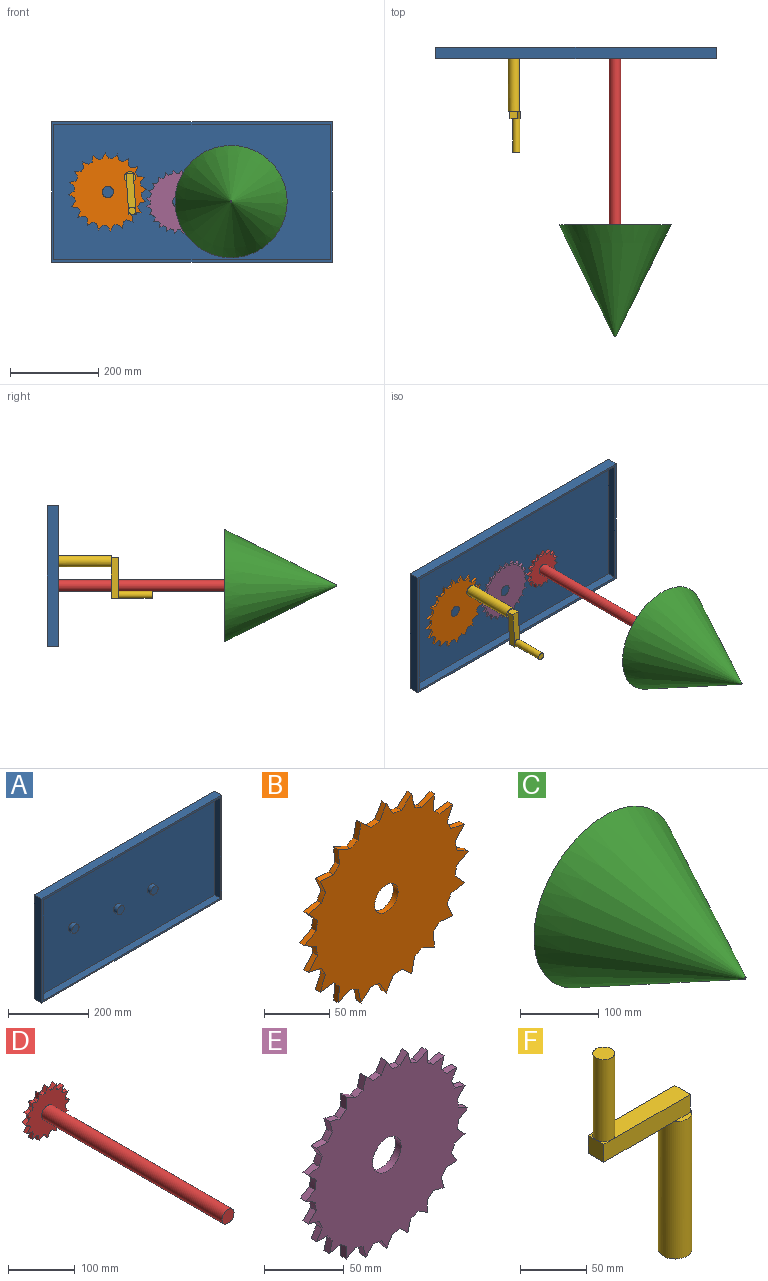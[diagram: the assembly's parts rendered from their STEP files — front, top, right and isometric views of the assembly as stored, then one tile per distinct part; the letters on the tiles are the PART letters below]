
ASSEMBLY  parts=6 mates=5
PART A: 17 faces, bbox 635x25.4x317.5 mm
  f0: plane 635x317.5mm, normal (0,-1,0), area 9574.2mm2, adj f1,f2,f3,f4,f6,f7,f8,f9
  f1: plane 317.5x25.4mm, normal (1,0,0), area 8064.5mm2, adj f0,f2,f4,f5
  f2: plane 635x25.4mm, normal (0,0,1), area 16129mm2, adj f0,f1,f3,f5
  f3: plane 317.5x25.4mm, normal (-1,0,0), area 8064.5mm2, adj f0,f2,f4,f5
  f4: plane 635x25.4mm, normal (0,0,-1), area 16129mm2, adj f0,f1,f3,f5
  f5: plane 635x317.5mm, normal (0,1,0), area 201612.5mm2, adj f1,f2,f3,f4
  f6: plane 307.34x20.32mm, normal (-1,0,0), area 6245.1mm2, adj f0,f7,f9,f10
  f7: plane 624.84x20.32mm, normal (0,0,-1), area 12696.7mm2, adj f0,f6,f8,f10
  f8: plane 307.34x20.32mm, normal (1,0,0), area 6245.1mm2, adj f0,f7,f9,f10
  f9: plane 624.84x20.32mm, normal (0,0,1), area 12696.7mm2, adj f0,f6,f8,f10
  f10: plane 624.84x307.34mm, normal (0,-1,0), area 190518.2mm2, adj f6,f7,f8,f9,f11,f13,f15
  f11: cylinder r=12.7mm len=25.4mm, axis (0,1,0), area 1013.4mm2, adj f10,f12
  f12: plane 25.4x25.4mm, normal (0,-1,0), area 506.7mm2, adj f11
  f13: cylinder r=12.7mm len=25.4mm, axis (0,1,0), area 1013.4mm2, adj f10,f14
  f14: plane 25.4x25.4mm, normal (0,-1,0), area 506.7mm2, adj f13
  f15: cylinder r=12.7mm len=25.4mm, axis (0,1,0), area 1013.4mm2, adj f10,f16
  f16: plane 25.4x25.4mm, normal (0,-1,0), area 506.7mm2, adj f15
PART B: 63 faces, bbox 177.4x5.1x177.4 mm
  f0: cylinder r=76.2mm len=8.92mm, axis (0,1,0), area 45.9mm2, adj f20,f21,f22,f60
  f1: cylinder r=76.2mm len=8.05mm, axis (0,1,0), area 45.9mm2, adj f20,f21,f58,f61
  f2: cylinder r=76.2mm len=6.39mm, axis (0,1,0), area 45.9mm2, adj f20,f21,f56,f59
  f3: cylinder r=76.2mm len=8.05mm, axis (0,1,0), area 45.9mm2, adj f20,f21,f54,f57
  f4: cylinder r=76.2mm len=8.92mm, axis (0,1,0), area 45.9mm2, adj f20,f21,f52,f55
  f5: cylinder r=76.2mm len=8.92mm, axis (0,1,0), area 45.9mm2, adj f20,f21,f50,f53
  f6: cylinder r=76.2mm len=8.05mm, axis (0,1,0), area 45.9mm2, adj f20,f21,f48,f51
  f7: cylinder r=76.2mm len=6.39mm, axis (0,1,0), area 45.9mm2, adj f20,f21,f46,f49
  f8: cylinder r=76.2mm len=8.05mm, axis (0,1,0), area 45.9mm2, adj f20,f21,f44,f47
  f9: cylinder r=76.2mm len=8.92mm, axis (0,1,0), area 45.9mm2, adj f20,f21,f42,f45
  f10: cylinder r=76.2mm len=8.92mm, axis (0,1,0), area 45.9mm2, adj f20,f21,f40,f43
  f11: cylinder r=76.2mm len=8.05mm, axis (0,1,0), area 45.9mm2, adj f20,f21,f38,f41
  f12: cylinder r=76.2mm len=6.39mm, axis (0,1,0), area 45.9mm2, adj f20,f21,f36,f39
  f13: cylinder r=76.2mm len=8.05mm, axis (0,1,0), area 45.9mm2, adj f20,f21,f34,f37
  f14: cylinder r=76.2mm len=8.92mm, axis (0,1,0), area 45.9mm2, adj f20,f21,f32,f35
  f15: cylinder r=76.2mm len=8.92mm, axis (0,1,0), area 45.9mm2, adj f20,f21,f30,f33
  f16: cylinder r=76.2mm len=8.05mm, axis (0,1,0), area 45.9mm2, adj f20,f21,f28,f31
  f17: cylinder r=76.2mm len=6.39mm, axis (0,1,0), area 45.9mm2, adj f20,f21,f26,f29
  f18: cylinder r=76.2mm len=8.05mm, axis (0,1,0), area 45.9mm2, adj f20,f21,f24,f27
  f19: cylinder r=76.2mm len=8.92mm, axis (0,1,0), area 45.9mm2, adj f20,f21,f23,f25
  f20: plane 177.44x177.44mm, normal (0,-1,0), area 19578.6mm2, adj f0,f1,f2,f3,f4,f5,f6,f7
  f21: plane 177.44x177.44mm, normal (0,1,0), area 19578.6mm2, adj f0,f1,f2,f3,f4,f5,f6,f7
  f22: plane 12.88x7.44mm, normal (0.87,0,0.5), area 75.6mm2, adj f0,f20,f21,f23
  f23: plane 12.88x7.44mm, normal (-0.87,0,0.5), area 75.6mm2, adj f19,f20,f21,f22
  f24: plane 14.55x5.08mm, normal (-0.98,0,0.21), area 75.6mm2, adj f18,f20,f21,f25
  f25: plane 11.05x9.95mm, normal (0.67,0,0.74), area 75.6mm2, adj f19,f20,f21,f24
  f26: plane 14.79x5.08mm, normal (-0.99,0,-0.1), area 75.6mm2, adj f17,f20,f21,f27
  f27: plane 13.59x6.05mm, normal (0.41,0,0.91), area 75.6mm2, adj f18,f20,f21,f26
  f28: plane 13.59x6.05mm, normal (-0.91,0,-0.41), area 75.6mm2, adj f16,f20,f21,f29
  f29: plane 14.79x5.08mm, normal (0.1,0,0.99), area 75.6mm2, adj f17,f20,f21,f28
  f30: plane 11.05x9.95mm, normal (-0.74,0,-0.67), area 75.6mm2, adj f15,f20,f21,f31
  f31: plane 14.55x5.08mm, normal (-0.21,0,0.98), area 75.6mm2, adj f16,f20,f21,f30
  f32: plane 12.88x7.44mm, normal (-0.5,0,-0.87), area 75.6mm2, adj f14,f20,f21,f33
  f33: plane 12.88x7.44mm, normal (-0.5,0,0.87), area 75.6mm2, adj f15,f20,f21,f32
  f34: plane 14.55x5.08mm, normal (-0.21,0,-0.98), area 75.6mm2, adj f13,f20,f21,f35
  f35: plane 11.05x9.95mm, normal (-0.74,0,0.67), area 75.6mm2, adj f14,f20,f21,f34
  f36: plane 14.79x5.08mm, normal (0.1,0,-0.99), area 75.6mm2, adj f12,f20,f21,f37
  f37: plane 13.59x6.05mm, normal (-0.91,0,0.41), area 75.6mm2, adj f13,f20,f21,f36
  f38: plane 13.59x6.05mm, normal (0.41,0,-0.91), area 75.6mm2, adj f11,f20,f21,f39
  f39: plane 14.79x5.08mm, normal (-0.99,0,0.1), area 75.6mm2, adj f12,f20,f21,f38
  f40: plane 11.05x9.95mm, normal (0.67,0,-0.74), area 75.6mm2, adj f10,f20,f21,f41
  f41: plane 14.55x5.08mm, normal (-0.98,0,-0.21), area 75.6mm2, adj f11,f20,f21,f40
  f42: plane 12.88x7.44mm, normal (0.87,0,-0.5), area 75.6mm2, adj f9,f20,f21,f43
  f43: plane 12.88x7.44mm, normal (-0.87,0,-0.5), area 75.6mm2, adj f10,f20,f21,f42
  f44: plane 14.55x5.08mm, normal (0.98,0,-0.21), area 75.6mm2, adj f8,f20,f21,f45
  f45: plane 11.05x9.95mm, normal (-0.67,0,-0.74), area 75.6mm2, adj f9,f20,f21,f44
  f46: plane 14.79x5.08mm, normal (0.99,0,0.1), area 75.6mm2, adj f7,f20,f21,f47
  f47: plane 13.59x6.05mm, normal (-0.41,0,-0.91), area 75.6mm2, adj f8,f20,f21,f46
  f48: plane 13.59x6.05mm, normal (0.91,0,0.41), area 75.6mm2, adj f6,f20,f21,f49
  f49: plane 14.79x5.08mm, normal (-0.1,0,-0.99), area 75.6mm2, adj f7,f20,f21,f48
  f50: plane 11.05x9.95mm, normal (0.74,0,0.67), area 75.6mm2, adj f5,f20,f21,f51
  f51: plane 14.55x5.08mm, normal (0.21,0,-0.98), area 75.6mm2, adj f6,f20,f21,f50
  f52: plane 12.88x7.44mm, normal (0.5,0,0.87), area 75.6mm2, adj f4,f20,f21,f53
  f53: plane 12.88x7.44mm, normal (0.5,0,-0.87), area 75.6mm2, adj f5,f20,f21,f52
  f54: plane 14.55x5.08mm, normal (0.21,0,0.98), area 75.6mm2, adj f3,f20,f21,f55
  f55: plane 11.05x9.95mm, normal (0.74,0,-0.67), area 75.6mm2, adj f4,f20,f21,f54
  f56: plane 14.79x5.08mm, normal (-0.1,0,0.99), area 75.6mm2, adj f2,f20,f21,f57
  f57: plane 13.59x6.05mm, normal (0.91,0,-0.41), area 75.6mm2, adj f3,f20,f21,f56
  f58: plane 13.59x6.05mm, normal (-0.41,0,0.91), area 75.6mm2, adj f1,f20,f21,f59
  f59: plane 14.79x5.08mm, normal (0.99,0,-0.1), area 75.6mm2, adj f2,f20,f21,f58
  f60: plane 11.05x9.95mm, normal (-0.67,0,0.74), area 75.6mm2, adj f0,f20,f21,f61
  f61: plane 14.55x5.08mm, normal (0.98,0,0.21), area 75.6mm2, adj f1,f20,f21,f60
  f62: cylinder r=12.7mm len=25.4mm, axis (0,-1,0), area 405.4mm2, adj f20,f21
PART C: 3 faces, bbox 254x254x254 mm
  f0: plane 254x254mm, normal (0,1,0), area 50670.7mm2, adj f2
  f1: plane 2.54x2.54mm, normal (0,-1,0), area 5.1mm2, adj f2
  f2: cone r=127mm half-angle=26.3deg, axis (0,1,0), area 114208.3mm2, adj f0,f1
PART D: 54 faces, bbox 93.1x388.6x93.1 mm
  f0: cylinder r=12.7mm len=25.4mm, axis (0,-1,0), area 405.4mm2, adj f17,f51
  f1: cylinder r=38.1mm len=7.62mm, axis (0,1,0), area 36.4mm2, adj f17,f47,f48,f50
  f2: cylinder r=38.1mm len=7.62mm, axis (0,1,0), area 36.4mm2, adj f17,f18,f49,f50
  f3: cylinder r=38.1mm len=7.62mm, axis (0,1,0), area 36.4mm2, adj f17,f45,f46,f50
  f4: cylinder r=38.1mm len=7.62mm, axis (0,1,0), area 36.4mm2, adj f17,f43,f44,f50
  f5: cylinder r=38.1mm len=7.62mm, axis (0,1,0), area 36.4mm2, adj f17,f41,f42,f50
  f6: cylinder r=38.1mm len=7.62mm, axis (0,1,0), area 36.4mm2, adj f17,f39,f40,f50
  f7: cylinder r=38.1mm len=7.62mm, axis (0,1,0), area 36.4mm2, adj f17,f37,f38,f50
  f8: cylinder r=38.1mm len=7.62mm, axis (0,1,0), area 36.4mm2, adj f17,f35,f36,f50
  f9: cylinder r=38.1mm len=7.62mm, axis (0,1,0), area 36.4mm2, adj f17,f33,f34,f50
  f10: cylinder r=38.1mm len=7.62mm, axis (0,1,0), area 36.4mm2, adj f17,f31,f32,f50
  f11: cylinder r=38.1mm len=7.62mm, axis (0,1,0), area 36.4mm2, adj f17,f29,f30,f50
  f12: cylinder r=38.1mm len=7.62mm, axis (0,1,0), area 36.4mm2, adj f17,f27,f28,f50
  f13: cylinder r=38.1mm len=7.62mm, axis (0,1,0), area 36.4mm2, adj f17,f25,f26,f50
  f14: cylinder r=38.1mm len=7.62mm, axis (0,1,0), area 36.4mm2, adj f17,f23,f24,f50
  f15: cylinder r=38.1mm len=7.62mm, axis (0,1,0), area 36.4mm2, adj f17,f21,f22,f50
  f16: cylinder r=38.1mm len=7.62mm, axis (0,1,0), area 36.4mm2, adj f17,f19,f20,f50
  f17: plane 93.12x93.12mm, normal (0,1,0), area 4731.9mm2, adj f0,f1,f2,f3,f4,f5,f6,f7
  f18: plane 8.8x7.62mm, normal (0.87,0,0.5), area 77.4mm2, adj f2,f17,f19,f50
  f19: plane 8.8x7.62mm, normal (-0.87,0,0.5), area 77.4mm2, adj f16,f17,f18,f50
  f20: plane 8.06x7.62mm, normal (0.61,0,0.79), area 77.4mm2, adj f16,f17,f21,f50
  f21: plane 10.07x7.62mm, normal (-0.99,0,0.13), area 77.4mm2, adj f15,f17,f20,f50
  f22: plane 9.81x7.62mm, normal (0.26,0,0.97), area 77.4mm2, adj f15,f17,f23,f50
  f23: plane 9.81x7.62mm, normal (-0.97,0,-0.26), area 77.4mm2, adj f14,f17,f22,f50
  f24: plane 10.07x7.62mm, normal (-0.13,0,0.99), area 77.4mm2, adj f14,f17,f25,f50
  f25: plane 8.06x7.62mm, normal (-0.79,0,-0.61), area 77.4mm2, adj f13,f17,f24,f50
  f26: plane 8.8x7.62mm, normal (-0.5,0,0.87), area 77.4mm2, adj f13,f17,f27,f50
  f27: plane 8.8x7.62mm, normal (-0.5,0,-0.87), area 77.4mm2, adj f12,f17,f26,f50
  f28: plane 8.06x7.62mm, normal (-0.79,0,0.61), area 77.4mm2, adj f12,f17,f29,f50
  f29: plane 10.07x7.62mm, normal (-0.13,0,-0.99), area 77.4mm2, adj f11,f17,f28,f50
  f30: plane 9.81x7.62mm, normal (-0.97,0,0.26), area 77.4mm2, adj f11,f17,f31,f50
  f31: plane 9.81x7.62mm, normal (0.26,0,-0.97), area 77.4mm2, adj f10,f17,f30,f50
  f32: plane 10.07x7.62mm, normal (-0.99,0,-0.13), area 77.4mm2, adj f10,f17,f33,f50
  f33: plane 8.06x7.62mm, normal (0.61,0,-0.79), area 77.4mm2, adj f9,f17,f32,f50
  f34: plane 8.8x7.62mm, normal (-0.87,0,-0.5), area 77.4mm2, adj f9,f17,f35,f50
  f35: plane 8.8x7.62mm, normal (0.87,0,-0.5), area 77.4mm2, adj f8,f17,f34,f50
  f36: plane 8.06x7.62mm, normal (-0.61,0,-0.79), area 77.4mm2, adj f8,f17,f37,f50
  f37: plane 10.07x7.62mm, normal (0.99,0,-0.13), area 77.4mm2, adj f7,f17,f36,f50
  f38: plane 9.81x7.62mm, normal (-0.26,0,-0.97), area 77.4mm2, adj f7,f17,f39,f50
  f39: plane 9.81x7.62mm, normal (0.97,0,0.26), area 77.4mm2, adj f6,f17,f38,f50
  f40: plane 10.07x7.62mm, normal (0.13,0,-0.99), area 77.4mm2, adj f6,f17,f41,f50
  f41: plane 8.06x7.62mm, normal (0.79,0,0.61), area 77.4mm2, adj f5,f17,f40,f50
  f42: plane 8.8x7.62mm, normal (0.5,0,-0.87), area 77.4mm2, adj f5,f17,f43,f50
  f43: plane 8.8x7.62mm, normal (0.5,0,0.87), area 77.4mm2, adj f4,f17,f42,f50
  f44: plane 8.06x7.62mm, normal (0.79,0,-0.61), area 77.4mm2, adj f4,f17,f45,f50
  f45: plane 10.07x7.62mm, normal (0.13,0,0.99), area 77.4mm2, adj f3,f17,f44,f50
  f46: plane 9.81x7.62mm, normal (0.97,0,-0.26), area 77.4mm2, adj f3,f17,f47,f50
  f47: plane 9.81x7.62mm, normal (-0.26,0,0.97), area 77.4mm2, adj f1,f17,f46,f50
  f48: plane 10.07x7.62mm, normal (0.99,0,0.13), area 77.4mm2, adj f1,f17,f49,f50
  f49: plane 8.06x7.62mm, normal (-0.61,0,0.79), area 77.4mm2, adj f2,f17,f48,f50
  f50: plane 93.12x93.12mm, normal (0,-1,0), area 4731.9mm2, adj f1,f2,f3,f4,f5,f6,f7,f8
  f51: plane 25.4x25.4mm, normal (0,1,0), area 506.7mm2, adj f0
  f52: cylinder r=12.7mm len=381mm, axis (0,1,0), area 30402.4mm2, adj f50,f53
  f53: plane 25.4x25.4mm, normal (0,-1,0), area 506.7mm2, adj f52
PART E: 75 faces, bbox 143.9x5.1x143.9 mm
  f0: cylinder r=63.81mm len=7.02mm, axis (0,1,0), area 36mm2, adj f24,f25,f27,f72
  f1: cylinder r=63.81mm len=6.54mm, axis (0,1,0), area 36mm2, adj f24,f25,f70,f73
  f2: cylinder r=63.81mm len=5.62mm, axis (0,1,0), area 36mm2, adj f24,f25,f68,f71
  f3: cylinder r=63.81mm len=5.62mm, axis (0,1,0), area 36mm2, adj f24,f25,f66,f69
  f4: cylinder r=63.81mm len=6.54mm, axis (0,1,0), area 36mm2, adj f24,f25,f64,f67
  f5: cylinder r=63.81mm len=7.02mm, axis (0,1,0), area 36mm2, adj f24,f25,f62,f65
  f6: cylinder r=63.81mm len=7.02mm, axis (0,1,0), area 36mm2, adj f24,f25,f60,f63
  f7: cylinder r=63.81mm len=6.54mm, axis (0,1,0), area 36mm2, adj f24,f25,f58,f61
  f8: cylinder r=63.81mm len=5.62mm, axis (0,1,0), area 36mm2, adj f24,f25,f56,f59
  f9: cylinder r=63.81mm len=5.62mm, axis (0,1,0), area 36mm2, adj f24,f25,f54,f57
  f10: cylinder r=63.81mm len=6.54mm, axis (0,1,0), area 36mm2, adj f24,f25,f52,f55
  f11: cylinder r=63.81mm len=7.02mm, axis (0,1,0), area 36mm2, adj f24,f25,f50,f53
  f12: cylinder r=63.81mm len=7.02mm, axis (0,1,0), area 36mm2, adj f24,f25,f48,f51
  f13: cylinder r=63.81mm len=6.54mm, axis (0,1,0), area 36mm2, adj f24,f25,f46,f49
  f14: cylinder r=63.81mm len=5.62mm, axis (0,1,0), area 36mm2, adj f24,f25,f44,f47
  f15: cylinder r=63.81mm len=5.62mm, axis (0,1,0), area 36mm2, adj f24,f25,f42,f45
  f16: cylinder r=63.81mm len=6.54mm, axis (0,1,0), area 36mm2, adj f24,f25,f40,f43
  f17: cylinder r=63.81mm len=7.02mm, axis (0,1,0), area 36mm2, adj f24,f25,f38,f41
  f18: cylinder r=63.81mm len=7.02mm, axis (0,1,0), area 36mm2, adj f24,f25,f36,f39
  f19: cylinder r=63.81mm len=6.54mm, axis (0,1,0), area 36mm2, adj f24,f25,f34,f37
  f20: cylinder r=63.81mm len=5.62mm, axis (0,1,0), area 36mm2, adj f24,f25,f32,f35
  f21: cylinder r=63.81mm len=5.62mm, axis (0,1,0), area 36mm2, adj f24,f25,f30,f33
  f22: cylinder r=63.81mm len=7.02mm, axis (0,1,0), area 36mm2, adj f24,f25,f26,f28
  f23: cylinder r=63.81mm len=6.54mm, axis (0,1,0), area 36mm2, adj f24,f25,f29,f31
  f24: plane 143.92x143.92mm, normal (0,-1,0), area 13219.3mm2, adj f0,f1,f2,f3,f4,f5,f6,f7
  f25: plane 143.92x143.92mm, normal (0,1,0), area 13219.3mm2, adj f0,f1,f2,f3,f4,f5,f6,f7
  f26: plane 8.33x5.08mm, normal (-0.87,0,0.5), area 48.8mm2, adj f22,f24,f25,f27
  f27: plane 8.33x5.08mm, normal (0.87,0,0.5), area 48.8mm2, adj f0,f24,f25,f26
  f28: plane 6.8x6.8mm, normal (0.71,0,0.71), area 48.8mm2, adj f22,f24,f25,f29
  f29: plane 9.29x5.08mm, normal (-0.97,0,0.26), area 48.8mm2, adj f23,f24,f25,f28
  f30: plane 9.61x5.08mm, normal (-1,0,0), area 48.8mm2, adj f21,f24,f25,f31
  f31: plane 8.33x5.08mm, normal (0.5,0,0.87), area 48.8mm2, adj f23,f24,f25,f30
  f32: plane 9.29x5.08mm, normal (-0.97,0,-0.26), area 48.8mm2, adj f20,f24,f25,f33
  f33: plane 9.29x5.08mm, normal (0.26,0,0.97), area 48.8mm2, adj f21,f24,f25,f32
  f34: plane 8.33x5.08mm, normal (-0.87,0,-0.5), area 48.8mm2, adj f19,f24,f25,f35
  f35: plane 9.61x5.08mm, normal (0,0,1), area 48.8mm2, adj f20,f24,f25,f34
  f36: plane 6.8x6.8mm, normal (-0.71,0,-0.71), area 48.8mm2, adj f18,f24,f25,f37
  f37: plane 9.29x5.08mm, normal (-0.26,0,0.97), area 48.8mm2, adj f19,f24,f25,f36
  f38: plane 8.33x5.08mm, normal (-0.5,0,-0.87), area 48.8mm2, adj f17,f24,f25,f39
  f39: plane 8.33x5.08mm, normal (-0.5,0,0.87), area 48.8mm2, adj f18,f24,f25,f38
  f40: plane 9.29x5.08mm, normal (-0.26,0,-0.97), area 48.8mm2, adj f16,f24,f25,f41
  f41: plane 6.8x6.8mm, normal (-0.71,0,0.71), area 48.8mm2, adj f17,f24,f25,f40
  f42: plane 9.61x5.08mm, normal (0,0,-1), area 48.8mm2, adj f15,f24,f25,f43
  f43: plane 8.33x5.08mm, normal (-0.87,0,0.5), area 48.8mm2, adj f16,f24,f25,f42
  f44: plane 9.29x5.08mm, normal (0.26,0,-0.97), area 48.8mm2, adj f14,f24,f25,f45
  f45: plane 9.29x5.08mm, normal (-0.97,0,0.26), area 48.8mm2, adj f15,f24,f25,f44
  f46: plane 8.33x5.08mm, normal (0.5,0,-0.87), area 48.8mm2, adj f13,f24,f25,f47
  f47: plane 9.61x5.08mm, normal (-1,0,0), area 48.8mm2, adj f14,f24,f25,f46
  f48: plane 6.8x6.8mm, normal (0.71,0,-0.71), area 48.8mm2, adj f12,f24,f25,f49
  f49: plane 9.29x5.08mm, normal (-0.97,0,-0.26), area 48.8mm2, adj f13,f24,f25,f48
  f50: plane 8.33x5.08mm, normal (0.87,0,-0.5), area 48.8mm2, adj f11,f24,f25,f51
  f51: plane 8.33x5.08mm, normal (-0.87,0,-0.5), area 48.8mm2, adj f12,f24,f25,f50
  f52: plane 9.29x5.08mm, normal (0.97,0,-0.26), area 48.8mm2, adj f10,f24,f25,f53
  f53: plane 6.8x6.8mm, normal (-0.71,0,-0.71), area 48.8mm2, adj f11,f24,f25,f52
  f54: plane 9.61x5.08mm, normal (1,0,0), area 48.8mm2, adj f9,f24,f25,f55
  f55: plane 8.33x5.08mm, normal (-0.5,0,-0.87), area 48.8mm2, adj f10,f24,f25,f54
  f56: plane 9.29x5.08mm, normal (0.97,0,0.26), area 48.8mm2, adj f8,f24,f25,f57
  f57: plane 9.29x5.08mm, normal (-0.26,0,-0.97), area 48.8mm2, adj f9,f24,f25,f56
  f58: plane 8.33x5.08mm, normal (0.87,0,0.5), area 48.8mm2, adj f7,f24,f25,f59
  f59: plane 9.61x5.08mm, normal (0,0,-1), area 48.8mm2, adj f8,f24,f25,f58
  f60: plane 6.8x6.8mm, normal (0.71,0,0.71), area 48.8mm2, adj f6,f24,f25,f61
  f61: plane 9.29x5.08mm, normal (0.26,0,-0.97), area 48.8mm2, adj f7,f24,f25,f60
  f62: plane 8.33x5.08mm, normal (0.5,0,0.87), area 48.8mm2, adj f5,f24,f25,f63
  f63: plane 8.33x5.08mm, normal (0.5,0,-0.87), area 48.8mm2, adj f6,f24,f25,f62
  f64: plane 9.29x5.08mm, normal (0.26,0,0.97), area 48.8mm2, adj f4,f24,f25,f65
  f65: plane 6.8x6.8mm, normal (0.71,0,-0.71), area 48.8mm2, adj f5,f24,f25,f64
  f66: plane 9.61x5.08mm, normal (0,0,1), area 48.8mm2, adj f3,f24,f25,f67
  f67: plane 8.33x5.08mm, normal (0.87,0,-0.5), area 48.8mm2, adj f4,f24,f25,f66
  f68: plane 9.29x5.08mm, normal (-0.26,0,0.97), area 48.8mm2, adj f2,f24,f25,f69
  f69: plane 9.29x5.08mm, normal (0.97,0,-0.26), area 48.8mm2, adj f3,f24,f25,f68
  f70: plane 8.33x5.08mm, normal (-0.5,0,0.87), area 48.8mm2, adj f1,f24,f25,f71
  f71: plane 9.61x5.08mm, normal (1,0,0), area 48.8mm2, adj f2,f24,f25,f70
  f72: plane 6.8x6.8mm, normal (-0.71,0,0.71), area 48.8mm2, adj f0,f24,f25,f73
  f73: plane 9.29x5.08mm, normal (0.97,0,0.26), area 48.8mm2, adj f1,f24,f25,f72
  f74: cylinder r=12.7mm len=25.4mm, axis (0,-1,0), area 405.4mm2, adj f24,f25
PART F: 13 faces, bbox 97.2x25.4x219.7 mm
  f0: plane 8.26x8.26mm, normal (0,0,1), area 14.6mm2, adj f6,f10,f11
  f1: plane 8.26x8.26mm, normal (0,0,1), area 14.6mm2, adj f7,f10,f11
  f2: plane 25.4x22.35mm, normal (0,0,1), area 176.6mm2, adj f3,f5,f6,f7
  f3: cylinder r=12.7mm len=127mm, axis (0,0,-1), area 10134.1mm2, adj f2,f4,f9
  f4: plane 25.4x25.4mm, normal (0,0,-1), area 506.7mm2, adj f3
  f5: plane 16.51x16.51mm, normal (1,0,0), area 272.6mm2, adj f2,f6,f7,f8
  f6: plane 92.71x16.51mm, normal (0,1,0), area 1530.6mm2, adj f0,f2,f5,f8,f9,f10
  f7: plane 92.71x16.51mm, normal (0,-1,0), area 1530.6mm2, adj f1,f2,f5,f8,f9,f10
  f8: plane 84.46x16.51mm, normal (0,0,1), area 1287.3mm2, adj f5,f6,f7,f11
  f9: plane 74.8x16.51mm, normal (0,0,-1), area 1200.6mm2, adj f3,f6,f7,f10
  f10: plane 16.51x16.51mm, normal (-1,0,0), area 272.6mm2, adj f0,f1,f6,f7,f9
  f11: cylinder r=8.26mm len=76.2mm, axis (0,0,-1), area 3952.3mm2, adj f0,f1,f8,f12
  f12: plane 16.51x16.51mm, normal (0,0,1), area 214.1mm2, adj f11
PLACE A t=(-11.08,11.81,8.27)mm fixed
PLACE B rot(axis=(0,1,0),86deg) t=(-201.58,-0.89,8.27)mm
PLACE C rot(axis=(0,1,0),51deg) t=(77.31,-389.51,-13.34)mm
PLACE D rot(axis=(0,-1,0),129deg) t=(77.31,-0.89,-13.34)mm
PLACE E rot(axis=(0,1,0),51deg) t=(-42.07,-0.89,-13.9)mm
PLACE F rot(axis=(0.55,-0.59,0.59),122.3deg) t=(-151.65,-5.97,41.68)mm
MATE revolute E.f0 <-> A.f13  axis (0,-1,0) through (-42.07,-5.97,-13.9)mm
MATE revolute D.f0 <-> A.f15  axis (0,1,0) through (77.31,-5.97,-13.34)mm
MATE fastened D.f0 <-> C.f2  axis (0,-1,0) through (77.31,-389.51,-13.34)mm
MATE revolute B.f62 <-> A.f11  axis (0,-1,0) through (-201.58,-5.97,8.27)mm
MATE fastened F.f3 <-> B.f20  axis (0,1,0) through (-151.65,-5.97,41.68)mm
